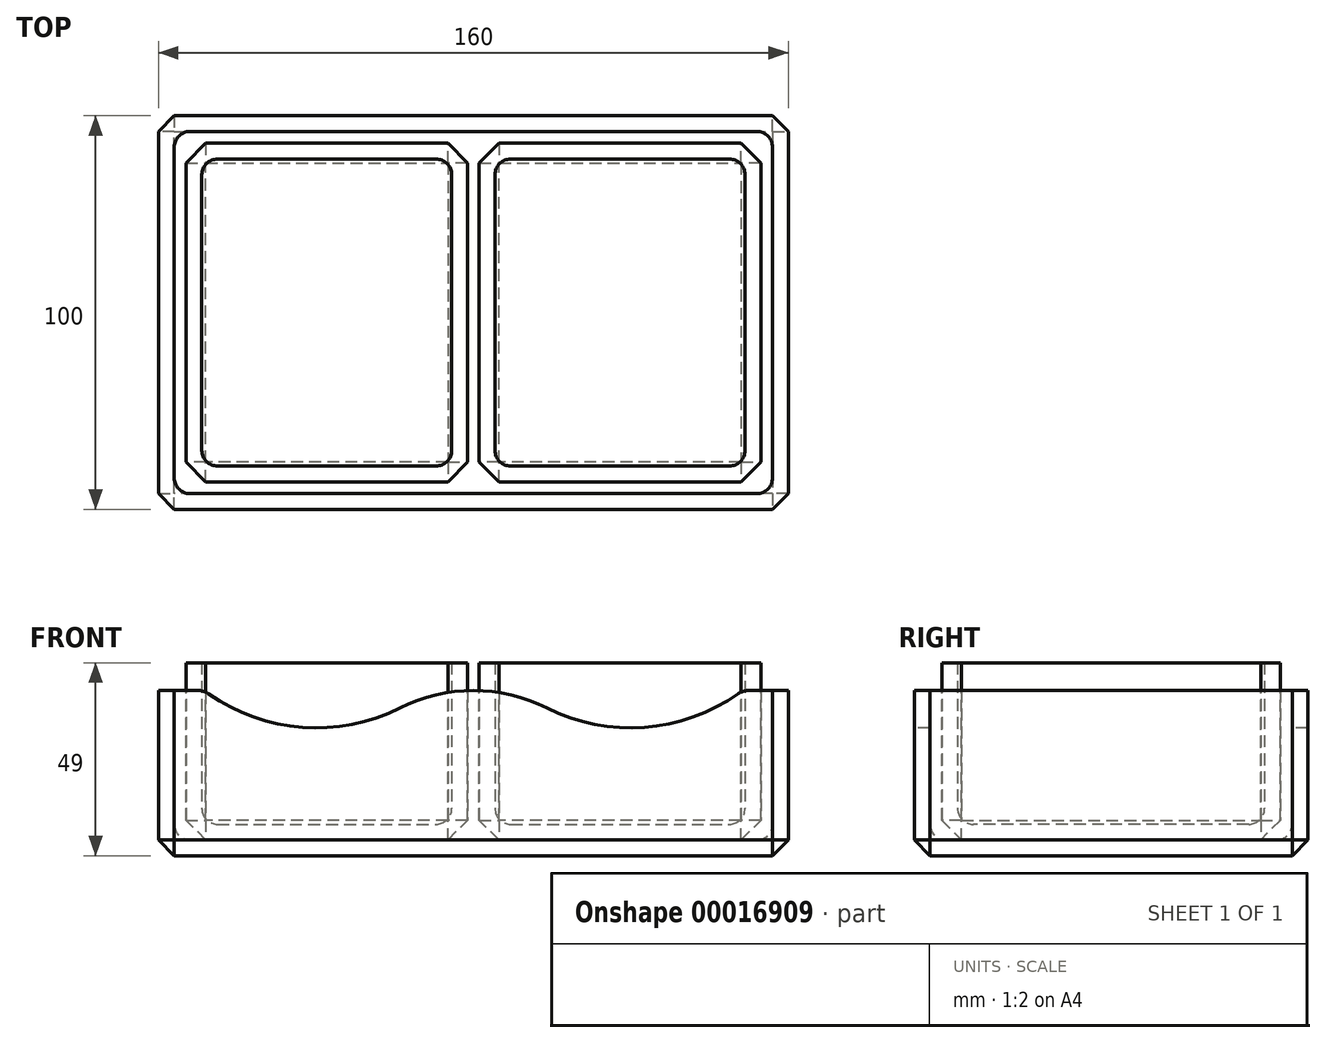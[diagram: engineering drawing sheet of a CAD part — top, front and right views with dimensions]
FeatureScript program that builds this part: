
annotation { "Feature Type Name" : "Feature", "Feature Type Description" : "" }
export const myFeature = defineFeature(function(context is Context, id is Id, definition is map)
    precondition{}
    {
        {
            var Q0;
            Q0=qCreatedBy(makeId("Front.planeOp"),FACE);
            var sketch = newSketch(context, id + "F0", { "sketchPlane" : qUnion([Q0])});
            skLineSegment(sketch, "E0.bottom", {"start": v(0, 0) * mm, "end": v(160, 0) * mm});
            skLineSegment(sketch, "E0.top", {"start": v(0, 42) * mm, "end": v(11.5, 42) * mm});
            skLineSegment(sketch, "E0.left", {"start": v(0, 0) * mm, "end": v(0, 42) * mm});
            skLineSegment(sketch, "E0.right", {"start": v(160, 0) * mm, "end": v(160, 42) * mm});
            skArc(sketch, "E1", {"start": v(11.5, 42) * mm, "mid": v(35.8, 32.69) * mm, "end": v(61.36, 37.57) * mm});
            skLineSegment(sketch, "E2", {"start": v(40, 80) * mm, "end": v(120, 80) * mm, "construction": true});
            skArc(sketch, "E3", {"start": v(98.64, 37.57) * mm, "mid": v(124.2, 32.69) * mm, "end": v(148.5, 42) * mm});
            skArc(sketch, "E4", {"start": v(98.64, 37.57) * mm, "mid": v(80, 42) * mm, "end": v(61.36, 37.57) * mm});
            skPoint(sketch, "E4.first.point", {"position": v(80, 42) * mm});
            skPoint(sketch, "E4.second.point", {"position": v(98.64, 37.57) * mm});
            skPoint(sketch, "E4.third.point", {"position": v(61.36, 37.57) * mm});
            skLineSegment(sketch, "E5.trimOffspring", {"start": v(148.5, 42) * mm, "end": v(160, 42) * mm});
            skLineSegment(sketch, "E6", {"start": v(80, 42) * mm, "end": v(148.5, 42) * mm, "construction": true});
            skLineSegment(sketch, "E7", {"start": v(11.5, 42) * mm, "end": v(80, 42) * mm, "construction": true});
            skSolve(sketch);
        }
        {
            var Q0;
            Q0=qSketchRegion(id+"F0",true);
            extrude(context, id + "F1", {"entities" : qUnion([Q0]), "oppositeDirection" : true, "depth" : 100 * mm});
        }
        {
            var Q0;
            Q0=makeQuery(id+"F1.opExtrude","SWEPT_FACE",FACE,{"disambiguationData":[OSD([sQuery(id+"F0.wireOp",EDGE,"E0.top")])]});
            var Q1;
            Q1=makeQuery(id+"F1.opExtrude","SWEPT_FACE",FACE,{"disambiguationData":[OSD([sQuery(id+"F0.wireOp",EDGE,"E1")])]});
            var Q2;
            Q2=makeQuery(id+"F1.opExtrude","SWEPT_FACE",FACE,{"disambiguationData":[OSD([sQuery(id+"F0.wireOp",EDGE,"E4")])]});
            var Q3;
            Q3=makeQuery(id+"F1.opExtrude","SWEPT_FACE",FACE,{"disambiguationData":[OSD([sQuery(id+"F0.wireOp",EDGE,"E3")])]});
            var Q4;
            Q4=makeQuery(id+"F1.opExtrude","SWEPT_FACE",FACE,{"disambiguationData":[OSD([sQuery(id+"F0.wireOp",EDGE,"E5.trimOffspring")])]});
            shell(context, id + "F2", {"entities" : qUnion([Q0, Q1, Q2, Q3, Q4]), "thickness" : 4 * mm});
        }
        {
            var Q0;
            {var subQ0=sQuery(id+"F0.wireOp",EDGE,"E0.right");Q0=makeQuery(id+"F2.opShell","OFFSET_EDGE",EDGE,{"disambiguationData":[OSD([subQ0]),TDD([makeQuery(id+"F1.opExtrude","CAP_EDGE",EDGE,{"disambiguationData":[OSD([subQ0])],"isStart":false})])]});}
            var Q1;
            {var subQ0=sQuery(id+"F0.wireOp",EDGE,"E0.left");Q1=makeQuery(id+"F2.opShell","OFFSET_EDGE",EDGE,{"disambiguationData":[OSD([subQ0]),TDD([makeQuery(id+"F1.opExtrude","CAP_EDGE",EDGE,{"disambiguationData":[OSD([subQ0])],"isStart":false})])]});}
            var Q2;
            {var subQ0=sQuery(id+"F0.wireOp",EDGE,"E0.left");Q2=makeQuery(id+"F2.opShell","OFFSET_EDGE",EDGE,{"disambiguationData":[OSD([subQ0]),TDD([makeQuery(id+"F1.opExtrude","CAP_EDGE",EDGE,{"disambiguationData":[OSD([subQ0])],"isStart":true})])]});}
            var Q3;
            {var subQ0=sQuery(id+"F0.wireOp",EDGE,"E0.right");Q3=makeQuery(id+"F2.opShell","OFFSET_EDGE",EDGE,{"disambiguationData":[OSD([subQ0]),TDD([makeQuery(id+"F1.opExtrude","CAP_EDGE",EDGE,{"disambiguationData":[OSD([subQ0])],"isStart":true})])]});}
            var Q4;
            {var subQ0=sQuery(id+"F0.wireOp",EDGE,"E0.bottom");Q4=makeQuery(id+"F2.opShell","OFFSET_EDGE",EDGE,{"disambiguationData":[OSD([subQ0]),TDD([makeQuery(id+"F1.opExtrude","CAP_EDGE",EDGE,{"disambiguationData":[OSD([subQ0])],"isStart":true})])]});}
            var Q5;
            Q5=makeQuery(id+"F2.opShell","OFFSET_EDGE",EDGE,{"disambiguationData":[OSD([sQuery(id+"F0.wireOp",EDGE,"E0.bottom"),sQuery(id+"F0.wireOp",EDGE,"E0.right")])]});
            var Q6;
            Q6=makeQuery(id+"F2.opShell","OFFSET_EDGE",EDGE,{"disambiguationData":[OSD([sQuery(id+"F0.wireOp",EDGE,"E0.bottom"),sQuery(id+"F0.wireOp",EDGE,"E0.left")])]});
            var Q7;
            {var subQ0=sQuery(id+"F0.wireOp",EDGE,"E0.bottom");Q7=makeQuery(id+"F2.opShell","OFFSET_EDGE",EDGE,{"disambiguationData":[OSD([subQ0]),TDD([makeQuery(id+"F1.opExtrude","CAP_EDGE",EDGE,{"disambiguationData":[OSD([subQ0])],"isStart":false})])]});}
            fillet(context, id + "F3", {"entities" : qUnion([Q0, Q1, Q2, Q3, Q4, Q5, Q6, Q7]), "radius" : 4 * mm, "tangentPropagation" : true, "allowEdgeOverflow" : false});
        }
        {
            var Q0;
            Q0=makeQuery(id+"F1.opExtrude","CAP_EDGE",EDGE,{"disambiguationData":[OSD([sQuery(id+"F0.wireOp",EDGE,"E0.right")])],"isStart":false});
            var Q1;
            Q1=makeQuery(id+"F1.opExtrude","CAP_EDGE",EDGE,{"disambiguationData":[OSD([sQuery(id+"F0.wireOp",EDGE,"E0.left")])],"isStart":false});
            var Q2;
            Q2=makeQuery(id+"F1.opExtrude","CAP_EDGE",EDGE,{"disambiguationData":[OSD([sQuery(id+"F0.wireOp",EDGE,"E0.right")])],"isStart":true});
            var Q3;
            Q3=makeQuery(id+"F1.opExtrude","CAP_EDGE",EDGE,{"disambiguationData":[OSD([sQuery(id+"F0.wireOp",EDGE,"E0.left")])],"isStart":true});
            var Q4;
            Q4=makeQuery(id+"F1.opExtrude","CAP_EDGE",EDGE,{"disambiguationData":[OSD([sQuery(id+"F0.wireOp",EDGE,"E0.bottom")])],"isStart":true});
            var Q5;
            Q5=makeQuery(id+"F1.opExtrude","SWEPT_EDGE",EDGE,{"disambiguationData":[OSD([sQuery(id+"F0.wireOp",EDGE,"E0.bottom"),sQuery(id+"F0.wireOp",EDGE,"E0.right")])]});
            var Q6;
            Q6=makeQuery(id+"F1.opExtrude","CAP_EDGE",EDGE,{"disambiguationData":[OSD([sQuery(id+"F0.wireOp",EDGE,"E0.bottom")])],"isStart":false});
            var Q7;
            Q7=makeQuery(id+"F1.opExtrude","SWEPT_EDGE",EDGE,{"disambiguationData":[OSD([sQuery(id+"F0.wireOp",EDGE,"E0.bottom"),sQuery(id+"F0.wireOp",EDGE,"E0.left")])]});
            chamfer(context, id + "F4", {"entities" : qUnion([Q0, Q1, Q2, Q3, Q4, Q5, Q6, Q7]), "width" : 4 * mm, "tangentPropagation" : true});
        }
        {
            var Q0;
            Q0=makeQuery(id+"F1.opExtrude","SWEPT_EDGE",EDGE,{"disambiguationData":[OSD([sQuery(id+"F0.wireOp",EDGE,"E3"),sQuery(id+"F0.wireOp",EDGE,"E5.trimOffspring")])]});
            var Q1;
            Q1=makeQuery(id+"F2.opShell","OFFSET_EDGE",EDGE,{"disambiguationData":[OSD([sQuery(id+"F0.wireOp",EDGE,"E3"),sQuery(id+"F0.wireOp",EDGE,"E5.trimOffspring")])]});
            var Q2;
            Q2=makeQuery(id+"F2.opShell","OFFSET_EDGE",EDGE,{"disambiguationData":[OSD([sQuery(id+"F0.wireOp",EDGE,"E0.top"),sQuery(id+"F0.wireOp",EDGE,"E1")])]});
            var Q3;
            Q3=makeQuery(id+"F1.opExtrude","SWEPT_EDGE",EDGE,{"disambiguationData":[OSD([sQuery(id+"F0.wireOp",EDGE,"E0.top"),sQuery(id+"F0.wireOp",EDGE,"E1")])]});
            fillet(context, id + "F5", {"entities" : qUnion([Q0, Q1, Q2, Q3]), "radius" : 5 * mm, "tangentPropagation" : true, "allowEdgeOverflow" : false});
        }
        {
            var Q0;
            Q0=makeQuery(id+"F2.opShell","OFFSET_FACE",FACE,{"disambiguationData":[OSD([sQuery(id+"F0.wireOp",EDGE,"E0.bottom")])]});
            var sketch = newSketch(context, id + "F6", { "sketchPlane" : qUnion([Q0])});
            skLineSegment(sketch, "E8.bottom", {"start": v(7, 93) * mm, "end": v(78.5, 93) * mm});
            skLineSegment(sketch, "E8.top", {"start": v(7, 7) * mm, "end": v(78.5, 7) * mm});
            skLineSegment(sketch, "E8.left", {"start": v(7, 93) * mm, "end": v(7, 7) * mm});
            skLineSegment(sketch, "E8.right", {"start": v(78.5, 93) * mm, "end": v(78.5, 7) * mm});
            skLineSegment(sketch, "E9", {"start": v(80, 92) * mm, "end": v(80, 8) * mm, "construction": true});
            skSolve(sketch);
        }
        {
            var Q0;
            Q0=qSketchRegion(id+"F6",true);
            extrude(context, id + "F7", {"entities" : qUnion([Q0]), "depth" : 45 * mm});
        }
        {
            var Q0;
            Q0=makeQuery(id+"F7.opExtrude","CAP_FACE",FACE,{"disambiguationData":[OSD([sQuery(id+"F6.wireOp",EDGE,"E8.bottom"),sQuery(id+"F6.wireOp",EDGE,"E8.top"),sQuery(id+"F6.wireOp",EDGE,"E8.left"),sQuery(id+"F6.wireOp",EDGE,"E8.right")])],"isStart":false});
            shell(context, id + "F8", {"entities" : qUnion([Q0]), "thickness" : 4 * mm});
        }
        {
            var Q0;
            Q0=makeQuery(id+"F8.opShell","OFFSET_EDGE",EDGE,{"disambiguationData":[OSD([sQuery(id+"F6.wireOp",EDGE,"E8.bottom"),sQuery(id+"F6.wireOp",EDGE,"E8.left")])]});
            var Q1;
            Q1=makeQuery(id+"F8.opShell","OFFSET_EDGE",EDGE,{"disambiguationData":[OSD([sQuery(id+"F6.wireOp",EDGE,"E8.bottom"),sQuery(id+"F6.wireOp",EDGE,"E8.right")])]});
            var Q2;
            Q2=makeQuery(id+"F8.opShell","OFFSET_EDGE",EDGE,{"disambiguationData":[OSD([sQuery(id+"F6.wireOp",EDGE,"E8.top"),sQuery(id+"F6.wireOp",EDGE,"E8.right")])]});
            var Q3;
            Q3=makeQuery(id+"F8.opShell","OFFSET_EDGE",EDGE,{"disambiguationData":[OSD([sQuery(id+"F6.wireOp",EDGE,"E8.top"),sQuery(id+"F6.wireOp",EDGE,"E8.left")])]});
            var Q4;
            {var subQ0=sQuery(id+"F6.wireOp",EDGE,"E8.right");Q4=makeQuery(id+"F8.opShell","OFFSET_EDGE",EDGE,{"disambiguationData":[OSD([subQ0]),TDD([makeQuery(id+"F7.opExtrude","CAP_EDGE",EDGE,{"disambiguationData":[OSD([subQ0])],"isStart":true})])]});}
            var Q5;
            {var subQ0=sQuery(id+"F6.wireOp",EDGE,"E8.bottom");Q5=makeQuery(id+"F8.opShell","OFFSET_EDGE",EDGE,{"disambiguationData":[OSD([subQ0]),TDD([makeQuery(id+"F7.opExtrude","CAP_EDGE",EDGE,{"disambiguationData":[OSD([subQ0])],"isStart":true})])]});}
            var Q6;
            {var subQ0=sQuery(id+"F6.wireOp",EDGE,"E8.top");Q6=makeQuery(id+"F8.opShell","OFFSET_EDGE",EDGE,{"disambiguationData":[OSD([subQ0]),TDD([makeQuery(id+"F7.opExtrude","CAP_EDGE",EDGE,{"disambiguationData":[OSD([subQ0])],"isStart":true})])]});}
            var Q7;
            {var subQ0=sQuery(id+"F6.wireOp",EDGE,"E8.left");Q7=makeQuery(id+"F8.opShell","OFFSET_EDGE",EDGE,{"disambiguationData":[OSD([subQ0]),TDD([makeQuery(id+"F7.opExtrude","CAP_EDGE",EDGE,{"disambiguationData":[OSD([subQ0])],"isStart":true})])]});}
            fillet(context, id + "F9", {"entities" : qUnion([Q0, Q1, Q2, Q3, Q4, Q5, Q6, Q7]), "radius" : 4 * mm, "tangentPropagation" : true, "allowEdgeOverflow" : false});
        }
        {
            var Q0;
            Q0=makeQuery(id+"F7.opExtrude","SWEPT_EDGE",EDGE,{"disambiguationData":[OSD([sQuery(id+"F6.wireOp",EDGE,"E8.top"),sQuery(id+"F6.wireOp",EDGE,"E8.left")])]});
            var Q1;
            Q1=makeQuery(id+"F7.opExtrude","CAP_EDGE",EDGE,{"disambiguationData":[OSD([sQuery(id+"F6.wireOp",EDGE,"E8.top")])],"isStart":true});
            var Q2;
            Q2=makeQuery(id+"F7.opExtrude","SWEPT_EDGE",EDGE,{"disambiguationData":[OSD([sQuery(id+"F6.wireOp",EDGE,"E8.top"),sQuery(id+"F6.wireOp",EDGE,"E8.right")])]});
            var Q3;
            Q3=makeQuery(id+"F7.opExtrude","CAP_EDGE",EDGE,{"disambiguationData":[OSD([sQuery(id+"F6.wireOp",EDGE,"E8.left")])],"isStart":true});
            var Q4;
            Q4=makeQuery(id+"F7.opExtrude","SWEPT_EDGE",EDGE,{"disambiguationData":[OSD([sQuery(id+"F6.wireOp",EDGE,"E8.bottom"),sQuery(id+"F6.wireOp",EDGE,"E8.left")])]});
            var Q5;
            Q5=makeQuery(id+"F7.opExtrude","CAP_EDGE",EDGE,{"disambiguationData":[OSD([sQuery(id+"F6.wireOp",EDGE,"E8.bottom")])],"isStart":true});
            var Q6;
            Q6=makeQuery(id+"F7.opExtrude","SWEPT_EDGE",EDGE,{"disambiguationData":[OSD([sQuery(id+"F6.wireOp",EDGE,"E8.bottom"),sQuery(id+"F6.wireOp",EDGE,"E8.right")])]});
            var Q7;
            Q7=makeQuery(id+"F7.opExtrude","CAP_EDGE",EDGE,{"disambiguationData":[OSD([sQuery(id+"F6.wireOp",EDGE,"E8.right")])],"isStart":true});
            chamfer(context, id + "F10", {"entities" : qUnion([Q0, Q1, Q2, Q3, Q4, Q5, Q6, Q7]), "width" : 5 * mm, "tangentPropagation" : true});
        }
        {
            var Q0;
            Q0=makeQuery(id+"F7.opExtrude","SWEPT_BODY",BODY,{"disambiguationData":[OSD([sQuery(id+"F6.wireOp",EDGE,"E8.bottom"),sQuery(id+"F6.wireOp",EDGE,"E8.top"),sQuery(id+"F6.wireOp",EDGE,"E8.left"),sQuery(id+"F6.wireOp",EDGE,"E8.right")])]});
            var Q1;
            {var subQ0=sQuery(id+"F0.wireOp",EDGE,"E0.bottom");Q1=makeQuery(id+"F4.opChamfer","BLEND_EDGE",EDGE,{"blendedFrom":[makeQuery(id+"F1.opExtrude","CAP_EDGE",EDGE,{"disambiguationData":[OSD([subQ0])],"isStart":true}),makeQuery(id+"F1.opExtrude","CAP_FACE",FACE,{"disambiguationData":[OSD([subQ0,sQuery(id+"F0.wireOp",EDGE,"E0.top"),sQuery(id+"F0.wireOp",EDGE,"E0.left"),sQuery(id+"F0.wireOp",EDGE,"E0.right"),sQuery(id+"F0.wireOp",EDGE,"E1"),sQuery(id+"F0.wireOp",EDGE,"E3"),sQuery(id+"F0.wireOp",EDGE,"E4"),sQuery(id+"F0.wireOp",EDGE,"E5.trimOffspring")])],"isStart":true})],"blendedInto":[makeQuery(id+"F1.opExtrude","CAP_FACE",FACE,{"disambiguationData":[OSD([subQ0,sQuery(id+"F0.wireOp",EDGE,"E0.top"),sQuery(id+"F0.wireOp",EDGE,"E0.left"),sQuery(id+"F0.wireOp",EDGE,"E0.right"),sQuery(id+"F0.wireOp",EDGE,"E1"),sQuery(id+"F0.wireOp",EDGE,"E3"),sQuery(id+"F0.wireOp",EDGE,"E4"),sQuery(id+"F0.wireOp",EDGE,"E5.trimOffspring")])],"isStart":true})]});}
            transform(context, id + "F11", {"entities" : qUnion([Q0]), "transformType" : TransformType.TRANSLATION_DISTANCE, "transformDirection" : qUnion([Q1]), "distance" : 74.5 * mm, "makeCopy" : true});
        }
    });
